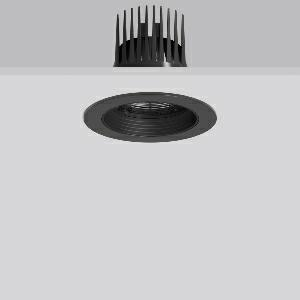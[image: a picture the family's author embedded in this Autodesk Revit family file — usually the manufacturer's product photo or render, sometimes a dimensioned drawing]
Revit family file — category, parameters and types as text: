
# Revit family: heledon_maxi_e_901761_003_1_f592
name_source: partatom
category: Lighting Fixtures
units: mm (PartAtom-declared; Revit-internal decimal feet)

## family parameters
Cut with Voids When Loaded = No
Host = Face
Light Source = No
Part Type = Normal
Room Calculation Point = No
Round Connector Dimension = Use Diameter
Shared = No

## types (1)
- HELEDON maxi E (1 x LED Modul 940, 2850 lm, 4000)
    Apparent Load = 25 VA
    Approval mark = CE
    CIE Flux Codes = 96 100 100 100 100
    Color Rendering = 92
    Color Temperature = 4000
    Default Elevation = 1800 mm
    Description = Series: HELEDON maxi
Round recessed downlight. Housing: die-cast aluminium, powder-coated. Black plastic ring and recessed LED to prevent glare from the side. Optical assembly with lens made of plastic (polycarbonate) for the best homogeneous light distribution - can be changed without tools. Best colour rendering index Ra>90. Suitable for Recessed ceiling mounting. Installation without tools thanks to spring fastening system. Including separate LED converter with connecting cable 600 mm.High quality converter without flickering and stroboscopic effect. Through-wiring box (5 pole) available as accessory. The following accessories can be mounted without use of tools: interchangeable lenses, decorative glasses, honeycomb louvre, clear and frosted diffusers, white interchangeable plastic ring. 
Colour: deep black, matt (RAL 9005)
Diameter: 162 mm
Height: 3 mm
Cut-out diameter: 152 mm
Recess height: 200 mm
Luminaire: recess height: 135 mm
Lamp: LED
Socket: without socket
Colour temperature: 4000K
Colour rendering index (CRI): 92
System power: 25 W
Rated luminous flux: 2850 lm
Luminous efficiency: 114 lm/W
Control gear: Regulated power supply
Protection class: II
Type of protection: IP 20
    Height = 0 mm  [stored 0 ft]
    Lamp = 1 x LED Modul 940
    Lamp Light Flux = 2850 lm
    Lamp count = 1
    Length = 162 mm
    Lifetime = 50000 h
    Luminous efficacy = 114 lm/W
    Manufacturer = RZB
    ModVariant = No
    Model = 901761.003.1
    Mounting Place = Ceiling
    Mounting Type = Recessed
    Number of Poles = 1
    OnlyDefault = Yes
    Power Factor = 1
    Product Name = HELEDON maxi E
    Product group = Recessed downlights
    ProductGroupID = 402
    Protection Class = Protection class II
    Protection Degree = IP 20
    RLX_Detail_Level = 1
    RLX_Emergency_Light_Flux = 0 lm
    RLX_Emergency_Type = 0
    RLX_Emergency_Type_DB = No
    RlxData = <blob elided: 119885 chars, md5=8499f679>
    Socket = socket
    Standby Power = 0 W
    System Light Flux = 2850 lm
    System Power = 25 W
    Type Comments = Product without accessories
    Type Image = 901663.003.jpg
    URL = http://relux.com
    VarID = ---
    Voltage = 230 V
    Voltage Range = 220-240 V
    Weight = 0.00 kg
    Width = 0 mm  [stored 0 ft]

note: [stored X ft] marks values corroborated as IEEE doubles in the binary element streams (Revit-internal decimal feet)

## geometry (parser evidence)
native form markers: Blend x4, Sweep x10
no freeform markers — native parametric forms only
